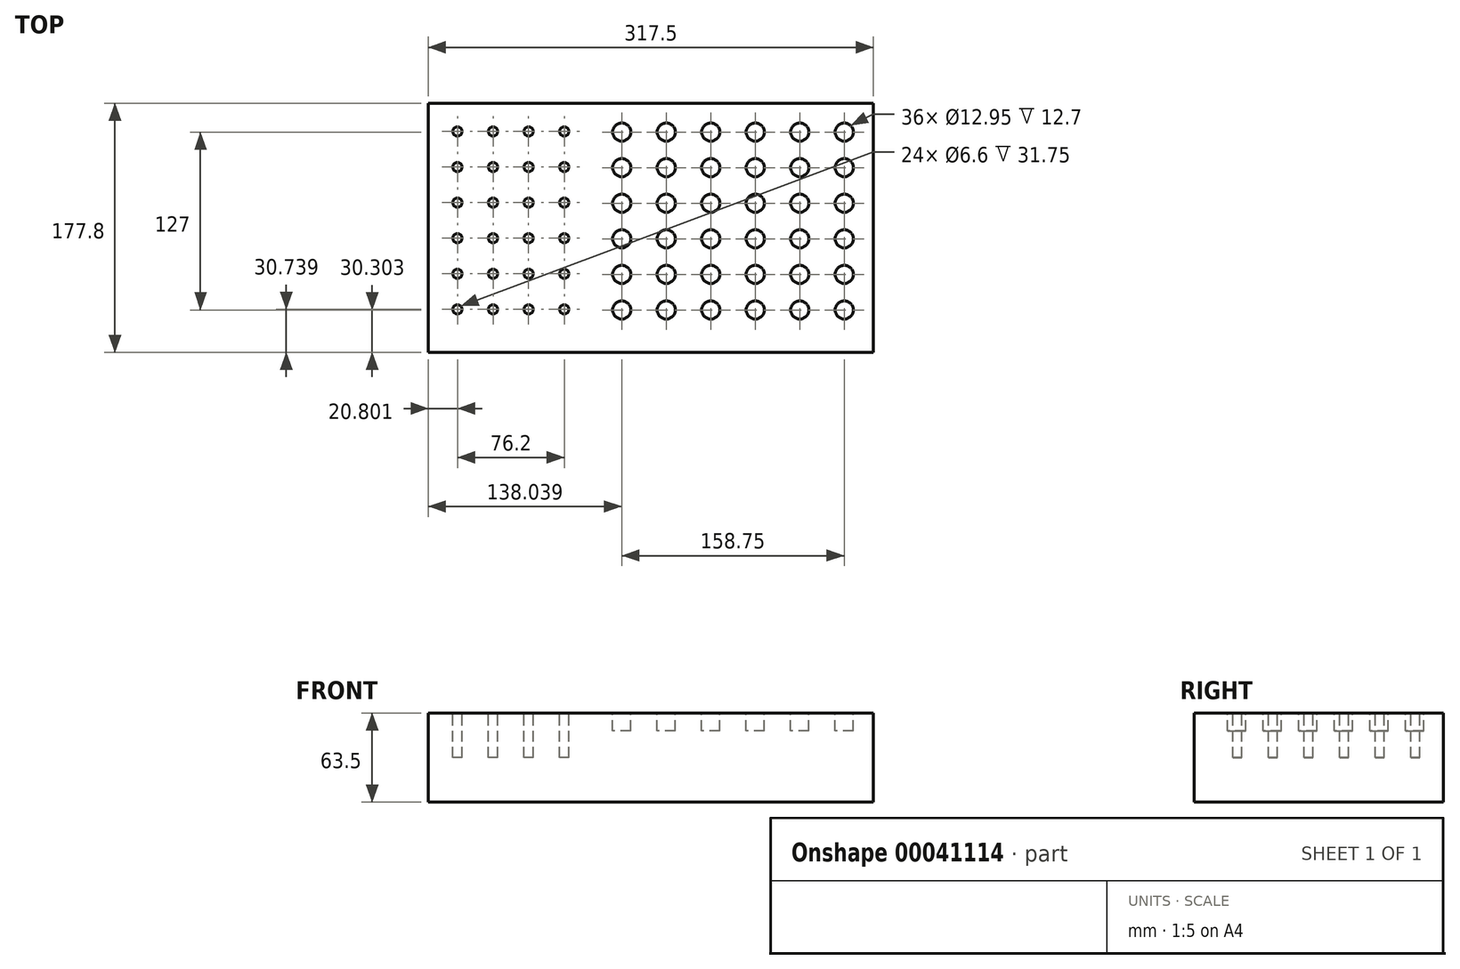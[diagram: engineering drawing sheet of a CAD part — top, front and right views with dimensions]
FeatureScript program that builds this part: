
annotation { "Feature Type Name" : "Feature", "Feature Type Description" : "" }
export const myFeature = defineFeature(function(context is Context, id is Id, definition is map)
    precondition{}
    {
        {
            var Q0;
            Q0=qCreatedBy(makeId("Top.planeOp"),FACE);
            var sketch = newSketch(context, id + "F0", { "sketchPlane" : qUnion([Q0])});
            skLineSegment(sketch, "E0.bottom", {"start": v(-135.29, 58.75) * mm, "end": v(182.21, 58.75) * mm});
            skLineSegment(sketch, "E0.top", {"start": v(-135.29, -119.05) * mm, "end": v(182.21, -119.05) * mm});
            skLineSegment(sketch, "E0.left", {"start": v(-135.29, 58.75) * mm, "end": v(-135.29, -119.05) * mm});
            skLineSegment(sketch, "E0.right", {"start": v(182.21, 58.75) * mm, "end": v(182.21, -119.05) * mm});
            skSolve(sketch);
        }
        {
            var Q0;
            Q0 = qSketchRegion(id + "F0", true);
            extrude(context, id + "F1", {"entities" : qUnion([Q0]), "depth" : 63.5 * mm});
        }
        {
            var Q0;
            Q0=makeQuery(id+"F1.opExtrude","CAP_FACE",FACE,{"disambiguationData":[OSD([sQuery(id+"F0.wireOp",EDGE,"E0.bottom"),sQuery(id+"F0.wireOp",EDGE,"E0.top"),sQuery(id+"F0.wireOp",EDGE,"E0.left"),sQuery(id+"F0.wireOp",EDGE,"E0.right")])],"isStart":false});
            var sketch = newSketch(context, id + "F2", { "sketchPlane" : qUnion([Q0])});
            skCircle(sketch, "E1", {"center": v(-114.49, 38.69) * mm, "radius": 3.3 * mm});
            skLineSegment(sketch, "E2", {"start": v(-114.49, 38.69) * mm, "end": v(-114.49, -119.05) * mm, "construction": true});
            skCircle(sketch, "E3.0.1.0", {"center": v(-114.49, 13.29) * mm, "radius": 3.3 * mm});
            skCircle(sketch, "E3.0.2.0", {"center": v(-114.49, -12.11) * mm, "radius": 3.3 * mm});
            skCircle(sketch, "E3.0.3.0", {"center": v(-114.49, -37.51) * mm, "radius": 3.3 * mm});
            skCircle(sketch, "E3.0.4.0", {"center": v(-114.49, -62.91) * mm, "radius": 3.3 * mm});
            skCircle(sketch, "E3.0.5.0", {"center": v(-114.49, -88.31) * mm, "radius": 3.3 * mm});
            skCircle(sketch, "E3.1.0.0", {"center": v(-89.09, 38.69) * mm, "radius": 3.3 * mm});
            skCircle(sketch, "E3.1.1.0", {"center": v(-89.09, 13.29) * mm, "radius": 3.3 * mm});
            skCircle(sketch, "E3.1.2.0", {"center": v(-89.09, -12.11) * mm, "radius": 3.3 * mm});
            skCircle(sketch, "E3.1.3.0", {"center": v(-89.09, -37.51) * mm, "radius": 3.3 * mm});
            skCircle(sketch, "E3.1.4.0", {"center": v(-89.09, -62.91) * mm, "radius": 3.3 * mm});
            skCircle(sketch, "E3.1.5.0", {"center": v(-89.09, -88.31) * mm, "radius": 3.3 * mm});
            skCircle(sketch, "E3.2.0.0", {"center": v(-63.69, 38.69) * mm, "radius": 3.3 * mm});
            skCircle(sketch, "E3.2.1.0", {"center": v(-63.69, 13.29) * mm, "radius": 3.3 * mm});
            skCircle(sketch, "E3.2.2.0", {"center": v(-63.69, -12.11) * mm, "radius": 3.3 * mm});
            skCircle(sketch, "E3.2.3.0", {"center": v(-63.69, -37.51) * mm, "radius": 3.3 * mm});
            skCircle(sketch, "E3.2.4.0", {"center": v(-63.69, -62.91) * mm, "radius": 3.3 * mm});
            skCircle(sketch, "E3.2.5.0", {"center": v(-63.69, -88.31) * mm, "radius": 3.3 * mm});
            skCircle(sketch, "E3.3.0.0", {"center": v(-38.29, 38.69) * mm, "radius": 3.3 * mm});
            skCircle(sketch, "E3.3.1.0", {"center": v(-38.29, 13.29) * mm, "radius": 3.3 * mm});
            skCircle(sketch, "E3.3.2.0", {"center": v(-38.29, -12.11) * mm, "radius": 3.3 * mm});
            skCircle(sketch, "E3.3.3.0", {"center": v(-38.29, -37.51) * mm, "radius": 3.3 * mm});
            skCircle(sketch, "E3.3.4.0", {"center": v(-38.29, -62.91) * mm, "radius": 3.3 * mm});
            skCircle(sketch, "E3.3.5.0", {"center": v(-38.29, -88.31) * mm, "radius": 3.3 * mm});
            skLineSegment(sketch, "E3.direction1", {"start": v(-114.49, 38.69) * mm, "end": v(-89.09, 38.69) * mm, "construction": true});
            skLineSegment(sketch, "E3.direction2", {"start": v(-114.49, 38.69) * mm, "end": v(-114.49, 13.29) * mm, "construction": true});
            skSolve(sketch);
        }
        {
            var Q0;
            Q0 = qSketchRegion(id + "F2", true);
            extrude(context, id + "F3", {"entities" : qUnion([Q0]), "operationType" : NewBodyOperationType.REMOVE, "oppositeDirection" : true, "depth" : 31.75 * mm});
        }
        {
            var Q0;
            Q0=makeQuery(id+"F1.opExtrude","CAP_FACE",FACE,{"disambiguationData":[OSD([sQuery(id+"F0.wireOp",EDGE,"E0.bottom"),sQuery(id+"F0.wireOp",EDGE,"E0.top"),sQuery(id+"F0.wireOp",EDGE,"E0.left"),sQuery(id+"F0.wireOp",EDGE,"E0.right")])],"isStart":false});
            var sketch = newSketch(context, id + "F4", { "sketchPlane" : qUnion([Q0])});
            skLineSegment(sketch, "E4", {"start": v(23.46, 58.75) * mm, "end": v(-156.2, -119.05) * mm, "construction": true});
            skCircle(sketch, "E5", {"center": v(2.75, 38.25) * mm, "radius": 6.48 * mm});
            skCircle(sketch, "E6.0.1.0", {"center": v(2.75, 12.85) * mm, "radius": 6.48 * mm});
            skCircle(sketch, "E6.0.2.0", {"center": v(2.75, -12.55) * mm, "radius": 6.48 * mm});
            skCircle(sketch, "E6.0.3.0", {"center": v(2.75, -37.95) * mm, "radius": 6.48 * mm});
            skCircle(sketch, "E6.0.4.0", {"center": v(2.75, -63.35) * mm, "radius": 6.48 * mm});
            skCircle(sketch, "E6.0.5.0", {"center": v(2.75, -88.75) * mm, "radius": 6.48 * mm});
            skCircle(sketch, "E6.1.0.0", {"center": v(34.5, 38.25) * mm, "radius": 6.48 * mm});
            skCircle(sketch, "E6.1.1.0", {"center": v(34.5, 12.85) * mm, "radius": 6.48 * mm});
            skCircle(sketch, "E6.1.2.0", {"center": v(34.5, -12.55) * mm, "radius": 6.48 * mm});
            skCircle(sketch, "E6.1.3.0", {"center": v(34.5, -37.95) * mm, "radius": 6.48 * mm});
            skCircle(sketch, "E6.1.4.0", {"center": v(34.5, -63.35) * mm, "radius": 6.48 * mm});
            skCircle(sketch, "E6.1.5.0", {"center": v(34.5, -88.75) * mm, "radius": 6.48 * mm});
            skCircle(sketch, "E6.2.0.0", {"center": v(66.25, 38.25) * mm, "radius": 6.48 * mm});
            skCircle(sketch, "E6.2.1.0", {"center": v(66.25, 12.85) * mm, "radius": 6.48 * mm});
            skCircle(sketch, "E6.2.2.0", {"center": v(66.25, -12.55) * mm, "radius": 6.48 * mm});
            skCircle(sketch, "E6.2.3.0", {"center": v(66.25, -37.95) * mm, "radius": 6.48 * mm});
            skCircle(sketch, "E6.2.4.0", {"center": v(66.25, -63.35) * mm, "radius": 6.48 * mm});
            skCircle(sketch, "E6.2.5.0", {"center": v(66.25, -88.75) * mm, "radius": 6.48 * mm});
            skCircle(sketch, "E6.3.0.0", {"center": v(98, 38.25) * mm, "radius": 6.48 * mm});
            skCircle(sketch, "E6.3.1.0", {"center": v(98, 12.85) * mm, "radius": 6.48 * mm});
            skCircle(sketch, "E6.3.2.0", {"center": v(98, -12.55) * mm, "radius": 6.48 * mm});
            skCircle(sketch, "E6.3.3.0", {"center": v(98, -37.95) * mm, "radius": 6.48 * mm});
            skCircle(sketch, "E6.3.4.0", {"center": v(98, -63.35) * mm, "radius": 6.48 * mm});
            skCircle(sketch, "E6.3.5.0", {"center": v(98, -88.75) * mm, "radius": 6.48 * mm});
            skCircle(sketch, "E6.4.0.0", {"center": v(129.75, 38.25) * mm, "radius": 6.48 * mm});
            skCircle(sketch, "E6.4.1.0", {"center": v(129.75, 12.85) * mm, "radius": 6.48 * mm});
            skCircle(sketch, "E6.4.2.0", {"center": v(129.75, -12.55) * mm, "radius": 6.48 * mm});
            skCircle(sketch, "E6.4.3.0", {"center": v(129.75, -37.95) * mm, "radius": 6.48 * mm});
            skCircle(sketch, "E6.4.4.0", {"center": v(129.75, -63.35) * mm, "radius": 6.48 * mm});
            skCircle(sketch, "E6.4.5.0", {"center": v(129.75, -88.75) * mm, "radius": 6.48 * mm});
            skCircle(sketch, "E6.5.0.0", {"center": v(161.5, 38.25) * mm, "radius": 6.48 * mm});
            skCircle(sketch, "E6.5.1.0", {"center": v(161.5, 12.85) * mm, "radius": 6.48 * mm});
            skCircle(sketch, "E6.5.2.0", {"center": v(161.5, -12.55) * mm, "radius": 6.48 * mm});
            skCircle(sketch, "E6.5.3.0", {"center": v(161.5, -37.95) * mm, "radius": 6.48 * mm});
            skCircle(sketch, "E6.5.4.0", {"center": v(161.5, -63.35) * mm, "radius": 6.48 * mm});
            skCircle(sketch, "E6.5.5.0", {"center": v(161.5, -88.75) * mm, "radius": 6.48 * mm});
            skLineSegment(sketch, "E6.direction1", {"start": v(2.75, 38.25) * mm, "end": v(34.5, 38.25) * mm, "construction": true});
            skLineSegment(sketch, "E6.direction2", {"start": v(2.75, 38.25) * mm, "end": v(2.75, 12.85) * mm, "construction": true});
            skSolve(sketch);
        }
        {
            var Q0;
            Q0 = qSketchRegion(id + "F4", true);
            extrude(context, id + "F5", {"entities" : qUnion([Q0]), "operationType" : NewBodyOperationType.REMOVE, "oppositeDirection" : true, "depth" : 12.7 * mm});
        }
    });
